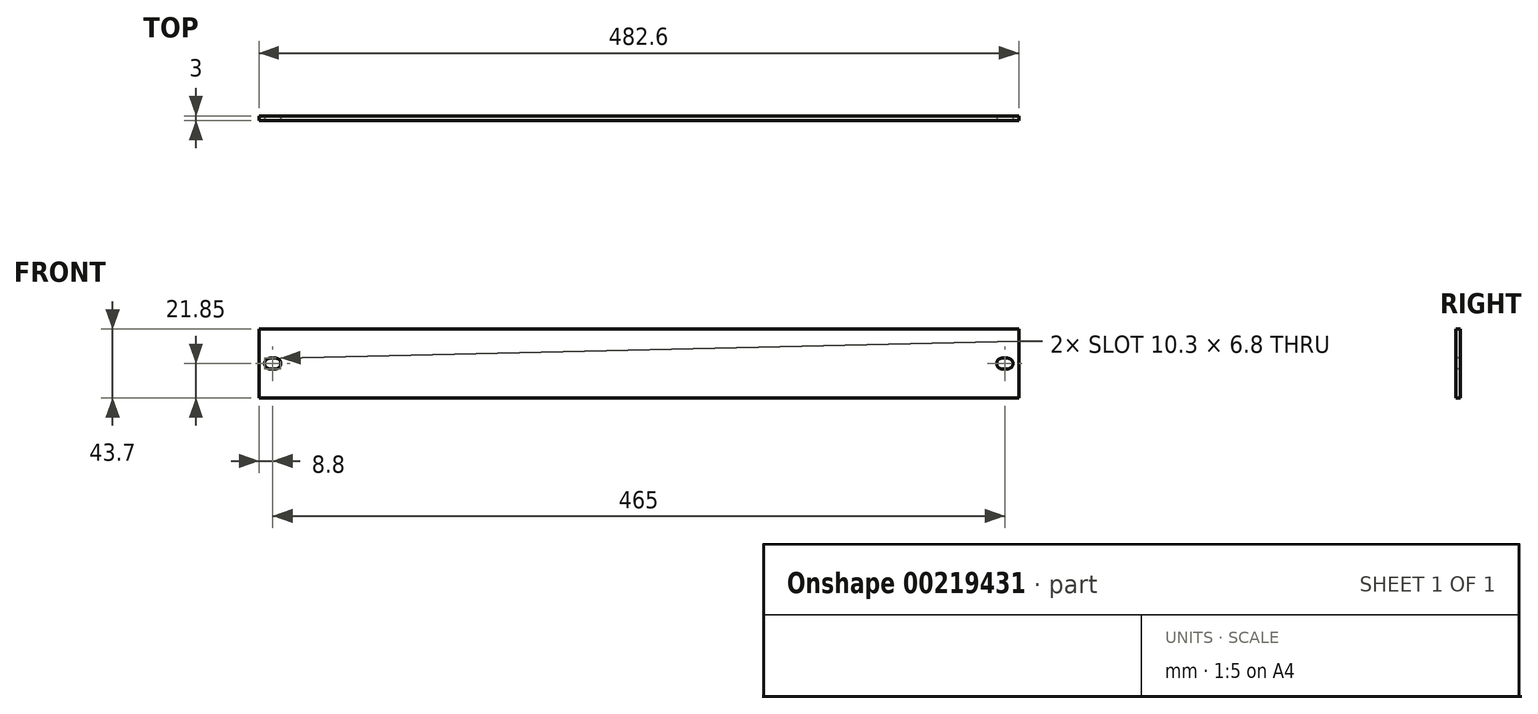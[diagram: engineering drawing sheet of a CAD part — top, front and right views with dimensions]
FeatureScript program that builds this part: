
annotation { "Feature Type Name" : "Feature", "Feature Type Description" : "" }
export const myFeature = defineFeature(function(context is Context, id is Id, definition is map)
    precondition{}
    {
        {
            var Q0;
            Q0=qCreatedBy(makeId("Front.planeOp"),FACE);
            var sketch = newSketch(context, id + "F0", { "sketchPlane" : qUnion([Q0])});
            skLineSegment(sketch, "E0.bottom", {"start": v(-241.3, -21.85) * mm, "end": v(241.3, -21.85) * mm});
            skLineSegment(sketch, "E0.top", {"start": v(-241.3, 21.85) * mm, "end": v(241.3, 21.85) * mm});
            skLineSegment(sketch, "E0.left", {"start": v(-241.3, -21.85) * mm, "end": v(-241.3, 21.85) * mm});
            skLineSegment(sketch, "E0.right", {"start": v(241.3, -21.85) * mm, "end": v(241.3, 21.85) * mm});
            skPoint(sketch, "E0.middle", {"position": v(0, 0) * mm});
            skSolve(sketch);
        }
        {
            var Q0;
            Q0=makeQuery(id+"F0.imprint","IMPRINT",FACE,{"disambiguationData":[TD([[makeQuery(id+"F0.imprint","IMPRINT",EDGE,{"derivedFrom":sQuery(id+"F0.wireOp",EDGE,"E0.bottom")}),1.0]])]});
            extrude(context, id + "F1", {"entities" : qUnion([Q0]), "oppositeDirection" : true, "depth" : 3 * mm});
        }
        {
            var Q0;
            Q0=makeQuery(id+"F1.opExtrude","CAP_FACE",FACE,{"disambiguationData":[OSD([sQuery(id+"F0.wireOp",EDGE,"E0.bottom"),sQuery(id+"F0.wireOp",EDGE,"E0.top"),sQuery(id+"F0.wireOp",EDGE,"E0.left"),sQuery(id+"F0.wireOp",EDGE,"E0.right")])],"isStart":true});
            var sketch = newSketch(context, id + "F2", { "sketchPlane" : qUnion([Q0])});
            skLineSegment(sketch, "E1.bottom", {"start": v(-230.75, -3.4) * mm, "end": v(-234.25, -3.4) * mm});
            skLineSegment(sketch, "E1.top", {"start": v(-230.75, 3.4) * mm, "end": v(-234.25, 3.4) * mm});
            skLineSegment(sketch, "E1.left", {"start": v(-230.75, -3.4) * mm, "end": v(-230.75, 3.4) * mm});
            skLineSegment(sketch, "E1.right", {"start": v(-234.25, -3.4) * mm, "end": v(-234.25, 3.4) * mm});
            skPoint(sketch, "E1.middle", {"position": v(-232.5, 0) * mm});
            skArc(sketch, "E2", {"start": v(-230.75, -3.4) * mm, "mid": v(-227.35, 0) * mm, "end": v(-230.75, 3.4) * mm});
            skArc(sketch, "E3", {"start": v(-234.25, 3.4) * mm, "mid": v(-237.65, 0) * mm, "end": v(-234.25, -3.4) * mm});
            skSolve(sketch);
        }
        {
            var Q0;
            Q0=makeQuery(id+"F2.imprint","IMPRINT",FACE,{"disambiguationData":[TD([[makeQuery(id+"F2.imprint","IMPRINT",EDGE,{"derivedFrom":sQuery(id+"F2.wireOp",EDGE,"E1.bottom")}),1.0]])]});
            var sketch = newSketch(context, id + "F3", { "sketchPlane" : qUnion([Q0])});
            skLineSegment(sketch, "E4.bottom", {"start": v(234.25, -3.4) * mm, "end": v(230.75, -3.4) * mm});
            skLineSegment(sketch, "E4.top", {"start": v(234.25, 3.4) * mm, "end": v(230.75, 3.4) * mm});
            skLineSegment(sketch, "E4.left", {"start": v(234.25, -3.4) * mm, "end": v(234.25, 3.4) * mm});
            skLineSegment(sketch, "E4.right", {"start": v(230.75, -3.4) * mm, "end": v(230.75, 3.4) * mm});
            skPoint(sketch, "E4.middle", {"position": v(232.5, 0) * mm});
            skArc(sketch, "E5", {"start": v(230.75, 3.4) * mm, "mid": v(227.35, 0) * mm, "end": v(230.75, -3.4) * mm});
            skArc(sketch, "E6", {"start": v(234.25, -3.4) * mm, "mid": v(237.65, 0) * mm, "end": v(234.25, 3.4) * mm});
            skSolve(sketch);
        }
        {
            var Q0;
            Q0=qSketchRegion(id+"F2",true);
            var Q1;
            Q1=qSketchRegion(id+"F3",true);
            extrude(context, id + "F4", {"entities" : qUnion([Q0, Q1]), "operationType" : NewBodyOperationType.REMOVE, "oppositeDirection" : true, "depth" : 3 * mm});
        }
    });
